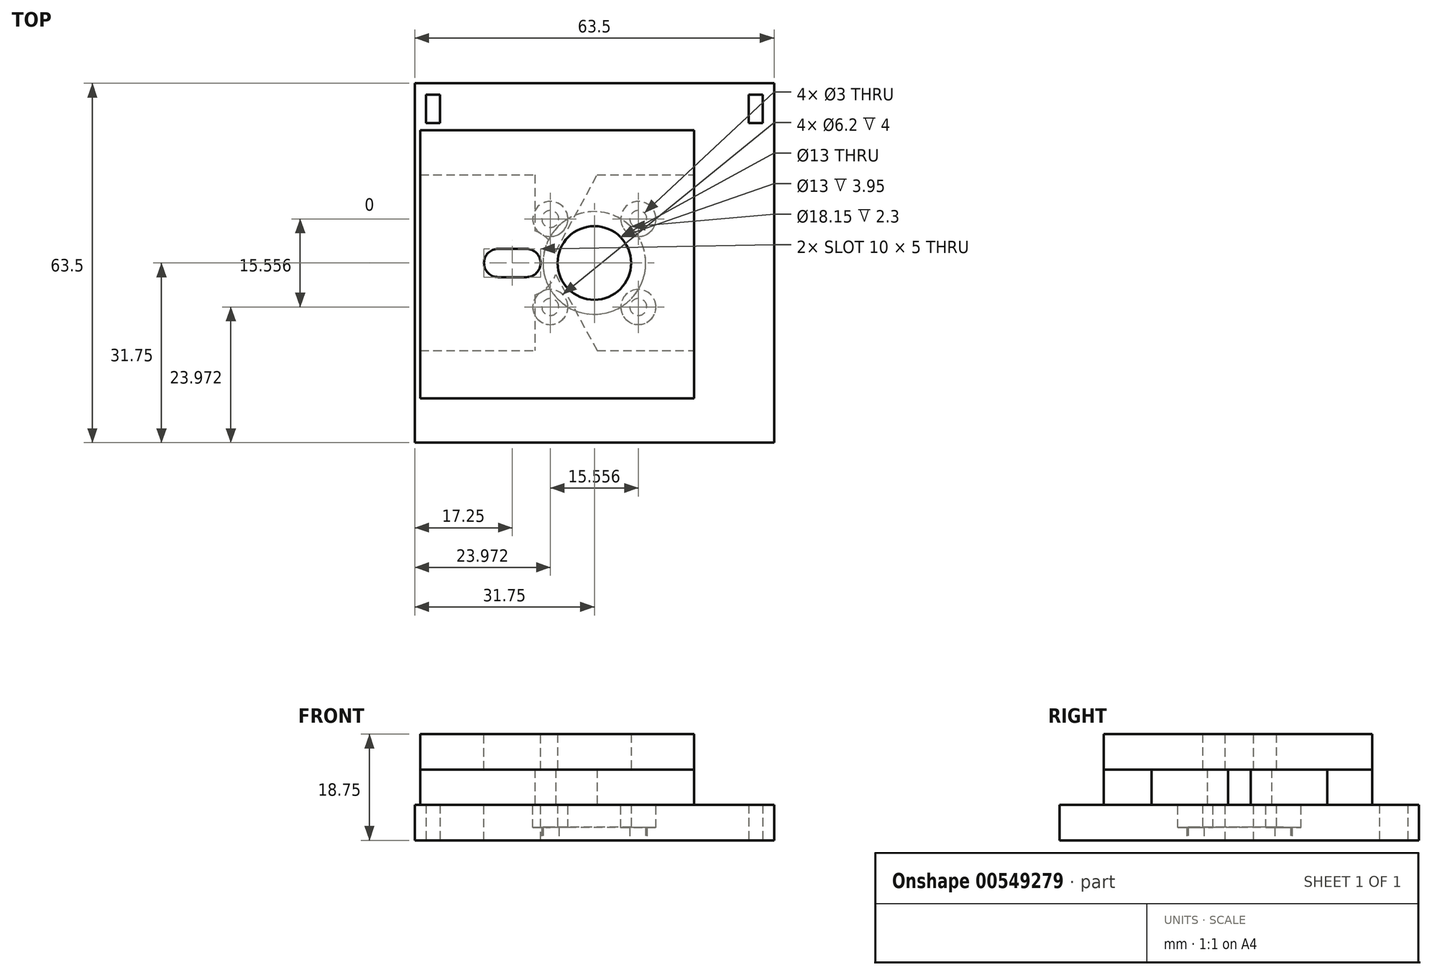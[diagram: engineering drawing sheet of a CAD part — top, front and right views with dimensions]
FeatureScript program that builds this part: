
annotation { "Feature Type Name" : "Feature", "Feature Type Description" : "" }
export const myFeature = defineFeature(function(context is Context, id is Id, definition is map)
    precondition{}
    {
        {
            assignVariable(context, id + "F0", {"name" : "baseT", "anyValue" : 6.25});
        }
        {
            assignVariable(context, id + "F1", {"name" : "m3BoltHeadRecess", "anyValue" : 4});
        }
        {
            assignVariable(context, id + "F2", {"name" : "stepperInsetH", "anyValue" : 2.3});
        }
        {
            var Q0;
            Q0=qCreatedBy(makeId("Top.planeOp"),FACE);
            var sketch = newSketch(context, id + "F3", { "sketchPlane" : qUnion([Q0])});
            skCircle(sketch, "E0", {"center": v(0, 0) * mm, "radius": 15 * mm, "construction": true});
            skLineSegment(sketch, "E1.bottom", {"start": v(-29.75, 29.75) * mm, "end": v(-27.25, 29.75) * mm});
            skLineSegment(sketch, "E1.top", {"start": v(-29.75, 24.75) * mm, "end": v(-27.25, 24.75) * mm});
            skLineSegment(sketch, "E1.left", {"start": v(-29.75, 29.75) * mm, "end": v(-29.75, 24.75) * mm});
            skLineSegment(sketch, "E1.right", {"start": v(-27.25, 29.75) * mm, "end": v(-27.25, 24.75) * mm});
            skLineSegment(sketch, "E2.bottom", {"start": v(29.75, 29.75) * mm, "end": v(27.25, 29.75) * mm});
            skLineSegment(sketch, "E2.top", {"start": v(29.75, 24.75) * mm, "end": v(27.25, 24.75) * mm});
            skLineSegment(sketch, "E2.left", {"start": v(29.75, 29.75) * mm, "end": v(29.75, 24.75) * mm});
            skLineSegment(sketch, "E2.right", {"start": v(27.25, 29.75) * mm, "end": v(27.25, 24.75) * mm});
            skLineSegment(sketch, "E3.1", {"start": v(-31.75, 31.75) * mm, "end": v(-31.75, -31.75) * mm});
            skLineSegment(sketch, "E3.2", {"start": v(-31.75, 31.75) * mm, "end": v(-27.25, 31.75) * mm});
            skLineSegment(sketch, "E4.0", {"start": v(31.75, 31.75) * mm, "end": v(27.25, 31.75) * mm});
            skLineSegment(sketch, "E4.1", {"start": v(31.75, 31.75) * mm, "end": v(31.75, -31.75) * mm});
            skLineSegment(sketch, "E5.right", {"start": v(-1, 28.46) * mm, "end": v(-1, -26.52) * mm, "construction": true});
            skLineSegment(sketch, "E6", {"start": v(-27.25, 31.75) * mm, "end": v(27.25, 31.75) * mm});
            skCircle(sketch, "E7", {"center": v(0, 0) * mm, "radius": 11 * mm, "construction": true});
            skCircle(sketch, "E8", {"center": v(-7.78, 7.78) * mm, "radius": 1.5 * mm});
            skCircle(sketch, "E9.1.0", {"center": v(-7.78, -7.78) * mm, "radius": 1.5 * mm});
            skCircle(sketch, "E9.2.0", {"center": v(7.78, -7.78) * mm, "radius": 1.5 * mm});
            skCircle(sketch, "E9.3.0", {"center": v(7.78, 7.78) * mm, "radius": 1.5 * mm});
            skCircle(sketch, "E10", {"center": v(-7.78, 7.78) * mm, "radius": 4.6 * mm, "construction": true});
            skCircle(sketch, "E11.1.0", {"center": v(-7.78, -7.78) * mm, "radius": 4.6 * mm, "construction": true});
            skCircle(sketch, "E11.2.0", {"center": v(7.78, -7.78) * mm, "radius": 4.6 * mm, "construction": true});
            skCircle(sketch, "E11.3.0", {"center": v(7.78, 7.78) * mm, "radius": 4.6 * mm, "construction": true});
            skLineSegment(sketch, "E12", {"start": v(31.75, -31.75) * mm, "end": v(-31.75, -31.75) * mm});
            skPoint(sketch, "E13.endSnap0", {"position": v(-27.25, 27.25) * mm});
            skCircle(sketch, "E14", {"center": v(0, 0) * mm, "radius": 6.5 * mm});
            skSolve(sketch);
        }
        {
            var Q0;
            Q0=makeQuery(id+"F3.imprint","IMPRINT",FACE,{"disambiguationData":[TD([[makeQuery(id+"F3.imprint","IMPRINT",EDGE,{"derivedFrom":sQuery(id+"F3.wireOp",EDGE,"E1.bottom")}),1.0]])]});
            extrude(context, id + "F4", {"entities" : qUnion([Q0]), "depth" : (getVariable(context, 'baseT')) * mm});
        }
        {
            var Q0;
            Q0=makeQuery(id+"F4.opExtrude","CAP_FACE",FACE,{"disambiguationData":[OSD([sQuery(id+"F3.wireOp",EDGE,"E1.bottom"),sQuery(id+"F3.wireOp",EDGE,"E1.top"),sQuery(id+"F3.wireOp",EDGE,"E1.left"),sQuery(id+"F3.wireOp",EDGE,"E1.right"),sQuery(id+"F3.wireOp",EDGE,"E2.bottom"),sQuery(id+"F3.wireOp",EDGE,"E2.top"),sQuery(id+"F3.wireOp",EDGE,"E2.left"),sQuery(id+"F3.wireOp",EDGE,"E2.right"),sQuery(id+"F3.wireOp",EDGE,"E3.0"),sQuery(id+"F3.wireOp",EDGE,"E3.1"),sQuery(id+"F3.wireOp",EDGE,"E3.2"),sQuery(id+"F3.wireOp",EDGE,"E4.0"),sQuery(id+"F3.wireOp",EDGE,"E4.1"),sQuery(id+"F3.wireOp",EDGE,"E4.2"),sQuery(id+"F3.wireOp",EDGE,"E6"),sQuery(id+"F3.wireOp",EDGE,"E8"),sQuery(id+"F3.wireOp",EDGE,"E9.1.0"),sQuery(id+"F3.wireOp",EDGE,"E9.2.0"),sQuery(id+"F3.wireOp",EDGE,"E9.3.0"),sQuery(id+"F3.wireOp",EDGE,"Mi6dx3AY-uMIZ-Df3I-gBde-4dB2NnZOwbx9"),sQuery(id+"F3.wireOp",EDGE,"E12"),sQuery(id+"F3.wireOp",EDGE,"He8D96uv-mS6Q-57cv-aHRz-I5kNUTtSJCBH"),sQuery(id+"F3.wireOp",EDGE,"E13"),sQuery(id+"F3.wireOp",EDGE,"wjEPWtgr-vBOl-Kljx-w1dd-p7NBxDcS8vAf"),sQuery(id+"F3.wireOp",EDGE,"PLWTT3C3-2iGu-kcem-znEJ-QKxlFtEV3tnr"),sQuery(id+"F3.wireOp",EDGE,"2zCN3ppK-VHyn-6Quy-Bxkh-GUdytJ533KvV"),sQuery(id+"F3.wireOp",EDGE,"iCG1O4UW-Ieoe-LlZV-2Yi0-UEBVlfb5CP1r"),sQuery(id+"F3.wireOp",EDGE,"E14")])],"isStart":false});
            var sketch = newSketch(context, id + "F5", { "sketchPlane" : qUnion([Q0])});
            skCircle(sketch, "E15", {"center": v(-7.78, 7.78) * mm, "radius": 3.1 * mm});
            skCircle(sketch, "E16.1.0", {"center": v(-7.78, -7.78) * mm, "radius": 3.1 * mm});
            skCircle(sketch, "E16.2.0", {"center": v(7.78, -7.78) * mm, "radius": 3.1 * mm});
            skCircle(sketch, "E16.3.0", {"center": v(7.78, 7.78) * mm, "radius": 3.1 * mm});
            skPoint(sketch, "E16.center", {"position": v(0, 0) * mm});
            skSolve(sketch);
        }
        {
            var Q0;
            Q0=qSketchRegion(id+"F5",true);
            extrude(context, id + "F6", {"entities" : qUnion([Q0]), "operationType" : NewBodyOperationType.REMOVE, "oppositeDirection" : true, "depth" : (getVariable(context, 'm3BoltHeadRecess')) * mm});
        }
        {
            var Q0;
            Q0=makeQuery(id+"F4.opExtrude","CAP_FACE",FACE,{"disambiguationData":[OSD([sQuery(id+"F3.wireOp",EDGE,"E1.bottom"),sQuery(id+"F3.wireOp",EDGE,"E1.top"),sQuery(id+"F3.wireOp",EDGE,"E1.left"),sQuery(id+"F3.wireOp",EDGE,"E1.right"),sQuery(id+"F3.wireOp",EDGE,"E2.bottom"),sQuery(id+"F3.wireOp",EDGE,"E2.top"),sQuery(id+"F3.wireOp",EDGE,"E2.left"),sQuery(id+"F3.wireOp",EDGE,"E2.right"),sQuery(id+"F3.wireOp",EDGE,"E3.0"),sQuery(id+"F3.wireOp",EDGE,"E3.1"),sQuery(id+"F3.wireOp",EDGE,"E3.2"),sQuery(id+"F3.wireOp",EDGE,"E4.0"),sQuery(id+"F3.wireOp",EDGE,"E4.1"),sQuery(id+"F3.wireOp",EDGE,"E4.2"),sQuery(id+"F3.wireOp",EDGE,"E6"),sQuery(id+"F3.wireOp",EDGE,"E8"),sQuery(id+"F3.wireOp",EDGE,"E9.1.0"),sQuery(id+"F3.wireOp",EDGE,"E9.2.0"),sQuery(id+"F3.wireOp",EDGE,"E9.3.0"),sQuery(id+"F3.wireOp",EDGE,"Mi6dx3AY-uMIZ-Df3I-gBde-4dB2NnZOwbx9"),sQuery(id+"F3.wireOp",EDGE,"E12"),sQuery(id+"F3.wireOp",EDGE,"He8D96uv-mS6Q-57cv-aHRz-I5kNUTtSJCBH"),sQuery(id+"F3.wireOp",EDGE,"E13"),sQuery(id+"F3.wireOp",EDGE,"wjEPWtgr-vBOl-Kljx-w1dd-p7NBxDcS8vAf"),sQuery(id+"F3.wireOp",EDGE,"PLWTT3C3-2iGu-kcem-znEJ-QKxlFtEV3tnr"),sQuery(id+"F3.wireOp",EDGE,"2zCN3ppK-VHyn-6Quy-Bxkh-GUdytJ533KvV"),sQuery(id+"F3.wireOp",EDGE,"iCG1O4UW-Ieoe-LlZV-2Yi0-UEBVlfb5CP1r"),sQuery(id+"F3.wireOp",EDGE,"E14")])],"isStart":true});
            var sketch = newSketch(context, id + "F7", { "sketchPlane" : qUnion([Q0])});
            skCircle(sketch, "E17", {"center": v(0, 0) * mm, "radius": 9.07 * mm});
            skSolve(sketch);
        }
        {
            var Q0;
            Q0=makeQuery(id+"F7.imprint","IMPRINT",FACE,{"disambiguationData":[TD([[makeQuery(id+"F7.imprint","IMPRINT",EDGE,{"derivedFrom":sQuery(id+"F7.wireOp",EDGE,"E17")}),1.0]])]});
            extrude(context, id + "F8", {"entities" : qUnion([Q0]), "operationType" : NewBodyOperationType.REMOVE, "oppositeDirection" : true, "depth" : (getVariable(context, 'stepperInsetH')) * mm});
        }
        {
            var Q0;
            Q0=makeQuery(id+"F4.opExtrude","CAP_FACE",FACE,{"disambiguationData":[OSD([sQuery(id+"F3.wireOp",EDGE,"E1.bottom"),sQuery(id+"F3.wireOp",EDGE,"E1.top"),sQuery(id+"F3.wireOp",EDGE,"E1.left"),sQuery(id+"F3.wireOp",EDGE,"E1.right"),sQuery(id+"F3.wireOp",EDGE,"E2.bottom"),sQuery(id+"F3.wireOp",EDGE,"E2.top"),sQuery(id+"F3.wireOp",EDGE,"E2.left"),sQuery(id+"F3.wireOp",EDGE,"E2.right"),sQuery(id+"F3.wireOp",EDGE,"E3.1"),sQuery(id+"F3.wireOp",EDGE,"E3.2"),sQuery(id+"F3.wireOp",EDGE,"E4.0"),sQuery(id+"F3.wireOp",EDGE,"E4.1"),sQuery(id+"F3.wireOp",EDGE,"E6"),sQuery(id+"F3.wireOp",EDGE,"E8"),sQuery(id+"F3.wireOp",EDGE,"E9.1.0"),sQuery(id+"F3.wireOp",EDGE,"E9.2.0"),sQuery(id+"F3.wireOp",EDGE,"E9.3.0"),sQuery(id+"F3.wireOp",EDGE,"E12"),sQuery(id+"F3.wireOp",EDGE,"E14")])],"isStart":false});
            var sketch = newSketch(context, id + "F9", { "sketchPlane" : qUnion([Q0])});
            skLineSegment(sketch, "E18.bottom", {"start": v(-30.75, -15.5) * mm, "end": v(17.62, -15.5) * mm});
            skLineSegment(sketch, "E18.top", {"start": v(-30.75, -23.95) * mm, "end": v(17.62, -23.95) * mm});
            skLineSegment(sketch, "E18.left", {"start": v(-30.75, -15.5) * mm, "end": v(-30.75, -23.95) * mm});
            skLineSegment(sketch, "E18.right", {"start": v(17.62, -15.5) * mm, "end": v(17.62, -23.95) * mm});
            skLineSegment(sketch, "E19.bottom", {"start": v(-30.75, 23.45) * mm, "end": v(17.62, 23.45) * mm});
            skLineSegment(sketch, "E19.top", {"start": v(-30.75, 15.55) * mm, "end": v(17.62, 15.55) * mm});
            skLineSegment(sketch, "E19.left", {"start": v(-30.75, 23.45) * mm, "end": v(-30.75, 15.55) * mm});
            skLineSegment(sketch, "E19.right", {"start": v(17.62, 23.45) * mm, "end": v(17.62, 15.55) * mm});
            skLineSegment(sketch, "E20", {"start": v(-10.5, 15.55) * mm, "end": v(-10.5, 5.66) * mm});
            skLineSegment(sketch, "E21", {"start": v(-10.5, -5.66) * mm, "end": v(-10.5, -15.5) * mm});
            skArc(sketch, "E22", {"start": v(-10.5, -5.66) * mm, "mid": v(-6.5, 0) * mm, "end": v(-10.5, 5.66) * mm});
            skLineSegment(sketch, "E23", {"start": v(-6.84, 2) * mm, "end": v(0.5, 15.55) * mm});
            skLineSegment(sketch, "E24", {"start": v(-6.84, -2) * mm, "end": v(0.5, -15.5) * mm});
            skSolve(sketch);
        }
        {
            var Q0;
            Q0=qSketchRegion(id+"F9",true);
            extrude(context, id + "F10", {"entities" : qUnion([Q0]), "depth" : (getVariable(context, 'baseT')) * mm});
        }
        {
            var Q0;
            Q0=makeQuery(id+"F10.opExtrude","CAP_FACE",FACE,{"disambiguationData":[OSD([sQuery(id+"F9.wireOp",EDGE,"E19.bottom"),sQuery(id+"F9.wireOp",EDGE,"E19.top"),sQuery(id+"F9.wireOp",EDGE,"E19.left"),sQuery(id+"F9.wireOp",EDGE,"E19.right")])],"isStart":false});
            var sketch = newSketch(context, id + "F11", { "sketchPlane" : qUnion([Q0])});
            skLineSegment(sketch, "E25.bottom", {"start": v(-30.75, 23.45) * mm, "end": v(17.62, 23.45) * mm});
            skLineSegment(sketch, "E25.top", {"start": v(-30.75, -23.95) * mm, "end": v(17.62, -23.95) * mm});
            skLineSegment(sketch, "E25.left", {"start": v(-30.75, 23.45) * mm, "end": v(-30.75, -23.95) * mm});
            skLineSegment(sketch, "E25.right", {"start": v(17.62, 23.45) * mm, "end": v(17.62, -23.95) * mm});
            skCircle(sketch, "E26", {"center": v(0, 0) * mm, "radius": 6.5 * mm});
            skSolve(sketch);
        }
        {
            var Q0;
            {var subQ0=sQuery(id+"F11.wireOp",EDGE,"E25.bottom");Q0=makeQuery(id+"F11.imprint","IMPRINT",FACE,{"disambiguationData":[TD([[makeQuery(id+"F11.imprint","IMPRINT",EDGE,{"derivedFrom":subQ0}),-1.0]])]});}
            var Q1;
            {var subQ0=sQuery(id+"F11.wireOp",EDGE,"E25.top");Q1=makeQuery(id+"F11.imprint","IMPRINT",FACE,{"disambiguationData":[TD([[makeQuery(id+"F11.imprint","IMPRINT",EDGE,{"derivedFrom":subQ0}),1.0]])]});}
            extrude(context, id + "F12", {"entities" : qUnion([Q0, Q1]), "depth" : (getVariable(context, 'baseT')) * mm});
        }
        {
            var Q0;
            Q0=makeQuery(id+"F12.opExtrude","CAP_FACE",FACE,{"disambiguationData":[OSD([sQuery(id+"F11.wireOp",EDGE,"E25.bottom"),sQuery(id+"F11.wireOp",EDGE,"E25.top"),sQuery(id+"F11.wireOp",EDGE,"E25.left"),sQuery(id+"F11.wireOp",EDGE,"E25.right"),sQuery(id+"F11.wireOp",EDGE,"E26")])],"isStart":false});
            var sketch = newSketch(context, id + "F13", { "sketchPlane" : qUnion([Q0])});
            skLineSegment(sketch, "E27", {"start": v(-17, 2.5) * mm, "end": v(-12, 2.5) * mm});
            skLineSegment(sketch, "E28", {"start": v(-17, -2.5) * mm, "end": v(-12, -2.5) * mm});
            skArc(sketch, "E29", {"start": v(-17, 2.5) * mm, "mid": v(-19.5, 0) * mm, "end": v(-17, -2.5) * mm});
            skArc(sketch, "E30", {"start": v(-12, -2.5) * mm, "mid": v(-9.5, 0) * mm, "end": v(-12, 2.5) * mm});
            skSolve(sketch);
        }
        {
            var Q0;
            Q0=qSketchRegion(id+"F13",true);
            extrude(context, id + "F14", {"entities" : qUnion([Q0]), "operationType" : NewBodyOperationType.REMOVE, "oppositeDirection" : true, "depth" : 25 * mm});
        }
    });
